# Revit family: Air Release Valve with check valve WE 2630 11 (12)
name_source: partatom
category: Rohrzubehör
revit_build: Autodesk Revit 2018 (Build: 20190510_1515(x64)
units: mm (PartAtom-declared; Revit-internal decimal feet)

## family parameters
Arbeitsebenenbasiert = Nein
Beim Laden mit Abzugskörper schneiden = Nein
Bemaßung runder Anschluss = Durchmesser verwenden
Gemeinsam genutzt = Nein
Immer vertikal = Ja
OmniClass-Nummer = 23.65.55.14
OmniClass-Titel = Valves for Liquid Services
Teiletyp = Normal

## types (1)
- Air Release Valve with check valve WE 2630 11 (12)
    Backflow preventer housing = brass CW617N, EN 12165
    Cover cap = ABS plastic, red colour
    D01 = 17.8 mm  [stored 0.0583989 ft]
    D02 = 20 mm
    D03 = 11 mm  [stored 0.0360892 ft]
    D04 = 12.5 mm  [stored 0.0410105 ft]
    D05 = 5.1 mm  [stored 0.0167323 ft]
    D06 = 3.4 mm  [stored 0.0111549 ft]
    D07 = 9 mm  [stored 0.0295276 ft]
    D08 = 4 mm  [stored 0.0131234 ft]
    External threaded connectors = acc. to ISO 228
    Field of application = HERZ - Air vent is used for venting of the central heating installations. The air vent should be placed nearby the boiler or at the highest points of installation. Installations must be carried out in such a way that the retention of air bubbles in a certain part of installation is not possible. Before usage, unscrew the polypropylene cover cap on the lid for 2 to 3 turns. In case of uncontrolled medium leakage, tighten the cover cap. The air vent must be cleaned or replaced. We always recommend to use backflow preventer for easy service and replacement of the air vent. The air vents 1 2630 1X have a STOP function that prevents the entry of ambient air into the central heating installation.
    Float ball = polypropylene
    G = 5 mm  [stored 0.0164042 ft]
    H00 = 56 mm  [stored 0.183727 ft]
    H01 = 9.5 mm  [stored 0.031168 ft]
    H02 = 13 mm
    H03 = 15.5 mm
    H04 = 14.5 mm
    H05 = 9 mm  [stored 0.0295276 ft]
    H06 = 2.5 mm  [stored 0.0082021 ft]
    H07 = 48.5 mm
    H08 = 55 mm  [stored 0.180446 ft]
    H10 = 2.5 mm  [stored 0.0082021 ft]
    H11 = 10 mm  [stored 0.0328084 ft]
    Hersteller = Herz-Armaturen GmbH
    Housing = machined brass acc. to EN 12165, CW617N
    L01 = 4 mm  [stored 0.0131234 ft]
    L02 = 28.3 mm
    L03 = 9.5 mm  [stored 0.031168 ft]
    L04 = 18.8 mm
    Lid = forged brass acc. to EN 12165, CW617N
    Medium = water purity in accordance with the ÖNORM H 5195 and VDI 2035 standards
    R01 = 1 mm  [stored 0.00328084 ft]
    R02 = 0.6 mm  [stored 0.0019685 ft]
    S01 = 56 mm  [stored 0.183727 ft]
    S02 = 11 mm  [stored 0.0360892 ft]
    S03 = 24.5 mm  [stored 0.0803806 ft]
    S04 = 16.5 mm  [stored 0.0541339 ft]
    S05 = 19 mm  [stored 0.062336 ft]
    SCRNCODE = 05;14;01
    SCRNSEQ = AWI;AWI_TYP="1013";1
    SW = 11 mm  [stored 0.0360892 ft]
    Sealing = EPDM
    URL = www.herzvalves.com
    max. Operating pressure = 1000000.0 Pa
    max. Operating temperature = 110 °C
    max. Structual pressure = 1000000.0 Pa
    min. Operating temperature = 0 °C

note: [stored X ft] marks values corroborated as IEEE doubles in the binary element streams (Revit-internal decimal feet)
